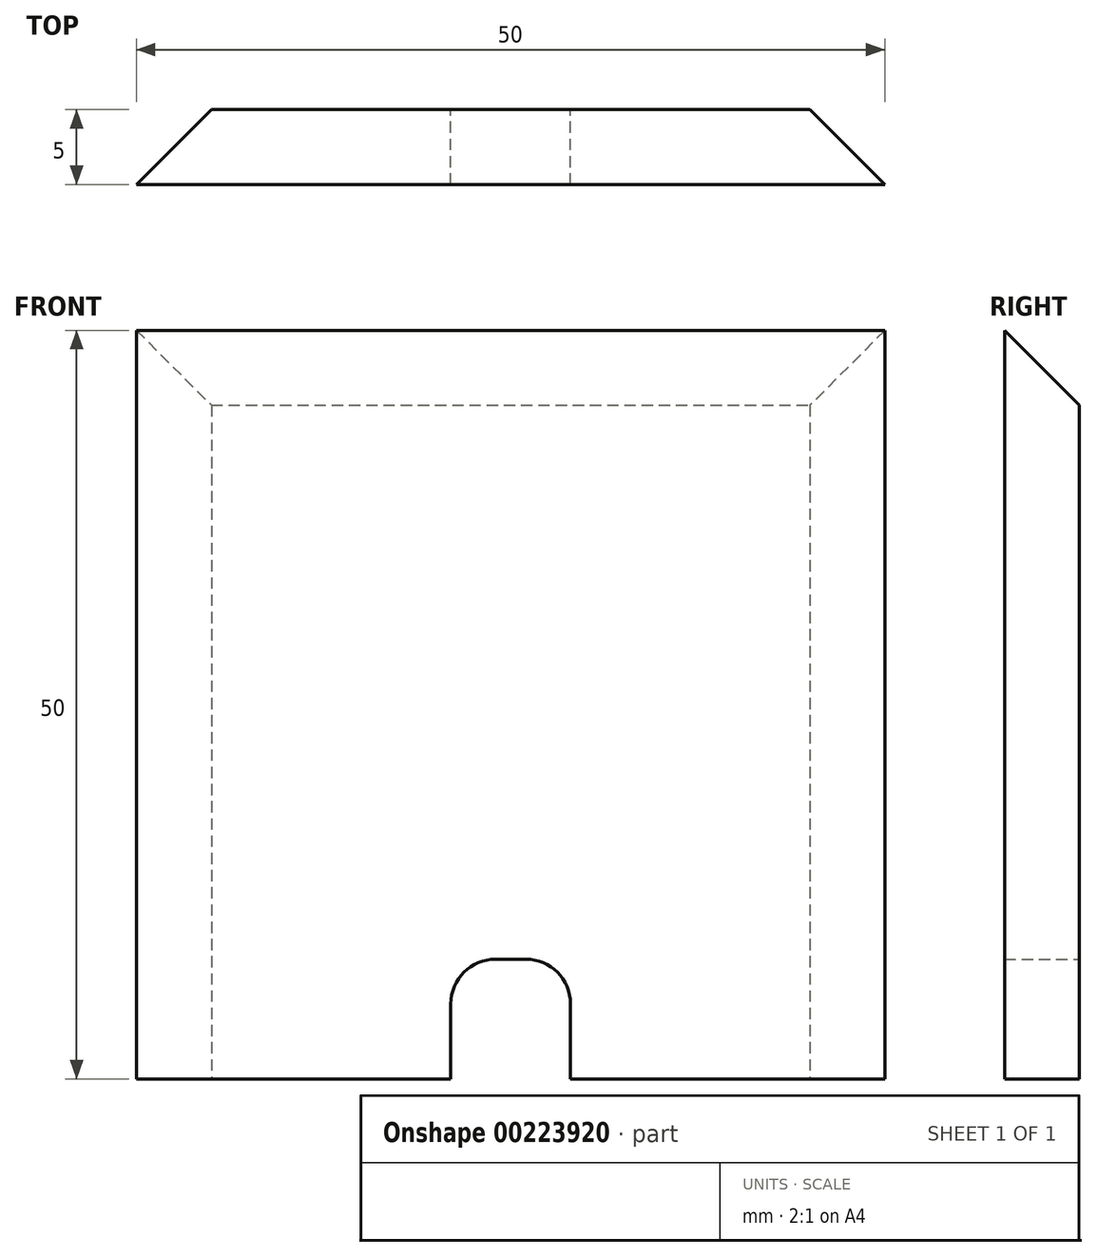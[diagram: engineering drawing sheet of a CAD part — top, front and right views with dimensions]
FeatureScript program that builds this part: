
annotation { "Feature Type Name" : "Feature", "Feature Type Description" : "" }
export const myFeature = defineFeature(function(context is Context, id is Id, definition is map)
    precondition{}
    {
        {
            var Q0;
            Q0=qCreatedBy(makeId("Front.planeOp"),FACE);
            var sketch = newSketch(context, id + "F0", { "sketchPlane" : qUnion([Q0])});
            skLineSegment(sketch, "E0.bottom", {"start": v(0, 0) * mm, "end": v(-50, 0) * mm});
            skLineSegment(sketch, "E0.top", {"start": v(0, 50) * mm, "end": v(-50, 50) * mm});
            skLineSegment(sketch, "E0.left", {"start": v(0, 0) * mm, "end": v(0, 50) * mm});
            skLineSegment(sketch, "E0.right", {"start": v(-50, 0) * mm, "end": v(-50, 50) * mm});
            skSolve(sketch);
        }
        {
            var Q0;
            Q0=makeQuery(id+"F0.imprint","IMPRINT",FACE,{"disambiguationData":[TD([[makeQuery(id+"F0.imprint","IMPRINT",EDGE,{"derivedFrom":sQuery(id+"F0.wireOp",EDGE,"E0.bottom")}),-1.0]])]});
            extrude(context, id + "F1", {"entities" : qUnion([Q0]), "depth" : 5 * mm});
        }
        {
            var Q0;
            Q0=makeQuery(id+"F1.opExtrude","SWEPT_FACE",FACE,{"disambiguationData":[OSD([sQuery(id+"F0.wireOp",EDGE,"E0.left")])]});
            var sketch = newSketch(context, id + "F2", { "sketchPlane" : qUnion([Q0])});
            skLineSegment(sketch, "E1", {"start": v(0, 50) * mm, "end": v(0, 45) * mm});
            skLineSegment(sketch, "E2", {"start": v(0, 45) * mm, "end": v(-5, 50) * mm});
            skSolve(sketch);
        }
        {
            var Q0;
            Q0 = qSketchRegion(id + "F2", true);
            var Q1;
            Q1=makeQuery(id+"F2.imprint","IMPRINT",FACE,{"disambiguationData":[TD([[makeQuery(id+"F2.imprint","IMPRINT",EDGE,{"derivedFrom":sQuery(id+"F2.wireOp",EDGE,"E1")}),1.0]])]});
            extrude(context, id + "F3", {"entities" : qUnion([Q0, Q1]), "operationType" : NewBodyOperationType.REMOVE, "oppositeDirection" : true, "depth" : 50 * mm});
        }
        {
            var Q0;
            Q0=makeQuery(id+"F1.opExtrude","SWEPT_FACE",FACE,{"disambiguationData":[OSD([sQuery(id+"F0.wireOp",EDGE,"E0.bottom")])]});
            var sketch = newSketch(context, id + "F4", { "sketchPlane" : qUnion([Q0])});
            skLineSegment(sketch, "E3", {"start": v(0, 0) * mm, "end": v(0, 5) * mm});
            skLineSegment(sketch, "E4", {"start": v(-5, 0) * mm, "end": v(0, 5) * mm});
            skLineSegment(sketch, "E5", {"start": v(-45, 0) * mm, "end": v(-50, 5) * mm});
            skSolve(sketch);
        }
        {
            var Q0;
            Q0 = qSketchRegion(id + "F4", true);
            var Q1;
            {var subQ0=sQuery(id+"F4.wireOp",EDGE,"E5");Q1=makeQuery(id+"F4.imprint","IMPRINT",FACE,{"disambiguationData":[TD([[makeQuery(id+"F4.imprint","IMPRINT",EDGE,{"derivedFrom":subQ0}),1.0]])]});}
            var Q2;
            {var subQ0=sQuery(id+"F4.wireOp",EDGE,"E3");Q2=makeQuery(id+"F4.imprint","IMPRINT",FACE,{"disambiguationData":[TD([[makeQuery(id+"F4.imprint","IMPRINT",EDGE,{"derivedFrom":subQ0}),-1.0]])]});}
            extrude(context, id + "F5", {"entities" : qUnion([Q0, Q1, Q2]), "operationType" : NewBodyOperationType.REMOVE, "oppositeDirection" : true, "depth" : 50 * mm});
        }
        {
            var Q0;
            Q0=makeQuery(id+"F1.opExtrude","CAP_FACE",FACE,{"disambiguationData":[OSD([sQuery(id+"F0.wireOp",EDGE,"E0.bottom"),sQuery(id+"F0.wireOp",EDGE,"E0.top"),sQuery(id+"F0.wireOp",EDGE,"E0.left"),sQuery(id+"F0.wireOp",EDGE,"E0.right")])],"isStart":true});
            var sketch = newSketch(context, id + "F6", { "sketchPlane" : qUnion([Q0])});
            skLineSegment(sketch, "E6", {"start": v(25, 0) * mm, "end": v(21, 0) * mm});
            skLineSegment(sketch, "E7", {"start": v(25, 0) * mm, "end": v(29, 0) * mm});
            skLineSegment(sketch, "E8", {"start": v(29, 0) * mm, "end": v(29, 8) * mm});
            skLineSegment(sketch, "E9", {"start": v(21, 0) * mm, "end": v(21, 8) * mm});
            skLineSegment(sketch, "E10", {"start": v(21, 8) * mm, "end": v(29, 8) * mm});
            skSolve(sketch);
        }
        {
            var Q0;
            Q0=makeQuery(id+"F6.imprint","IMPRINT",FACE,{"disambiguationData":[TD([[makeQuery(id+"F6.imprint","IMPRINT",EDGE,{"derivedFrom":sQuery(id+"F6.wireOp",EDGE,"E6")}),1.0]])]});
            extrude(context, id + "F7", {"entities" : qUnion([Q0]), "operationType" : NewBodyOperationType.REMOVE, "oppositeDirection" : true, "depth" : 25 * mm});
        }
        {
            var Q0;
            Q0=makeQuery(id+"F7.boolean.opBoolean","COPY",EDGE,{"derivedFrom":makeQuery(id+"F7.opExtrude","SWEPT_EDGE",EDGE,{"disambiguationData":[OSD([sQuery(id+"F6.wireOp",EDGE,"E9"),sQuery(id+"F6.wireOp",EDGE,"E10")])]})});
            var Q1;
            Q1=makeQuery(id+"F7.boolean.opBoolean","COPY",EDGE,{"derivedFrom":makeQuery(id+"F7.opExtrude","SWEPT_EDGE",EDGE,{"disambiguationData":[OSD([sQuery(id+"F6.wireOp",EDGE,"E8"),sQuery(id+"F6.wireOp",EDGE,"E10")])]})});
            fillet(context, id + "F8", {"entities" : qUnion([Q0, Q1]), "radius" : 3 * mm, "tangentPropagation" : true, "allowEdgeOverflow" : false});
        }
    });
